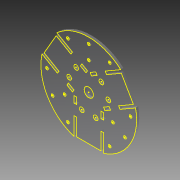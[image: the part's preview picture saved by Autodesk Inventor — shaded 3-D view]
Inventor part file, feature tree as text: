
AUTODESK INVENTOR PART (.ipt)
format: ipt  version: 2015 (Build 190159000, 159)  size: 303,616 bytes
history: native  units: mm
features: sketch x8, extrude x6, projected_geometry x4, pattern_circular x2
ambient origin geometry x8: Origin, YZ Plane, XZ Plane, XY Plane, X Axis, Y Axis, Z Axis, Center Point
bodies: Solid1 (feature_tree)
feature tree (20):
  extrude  "Extrusion1"  Depth=3.0mm TaperAngle=0.0deg
  extrude  "Extrusion2"  Depth=7.0mm
  extrude  "Extrusion3"  Depth=11.724mm
  extrude  "Extrusion4"  Depth=3.0mm
  extrude  "Extrusion5"  Depth=3.0mm TaperAngle=0.0deg
  pattern_circular  "Circular Pattern1"  [2 undecoded]
  sketch  "Sketch6"  dims[d12=5.0mm]
  pattern_circular  "Circular Pattern2"  [2 undecoded]
  extrude  "Extrusion6"  Depth=3.0mm TaperAngle=0.0deg
  sketch  "Sketch8"  dims[d14=20.006mm d15=5.0mm d16=3.0mm d17=0.0mm d18=3.0mm d19=0.0mm d20=48.0mm d21=10.0mm d22=3.0mm d23=0.0mm d24=30.0mm d25=360.0deg d27=30.0mm d28=360.0deg d30=60.0mm d31=90.0mm d32=30.0deg d33=30.0deg d34=30.0deg d35=30.0deg d36=30.0deg d37=30.0deg d38=120.0deg d39=120.0deg d40=3.0mm d41=3.0mm d42=3.0mm d43=3.0mm d44=3.0mm d45=3.0mm d46=3.0mm d47=3.0mm d48=3.0mm d49=3.0mm d50=3.0mm d51=3.0mm d52=3.0mm d53=0.0mm]
  sketch  "Sketch1"  dims[d0=103.0mm d1=3.0mm d2=0.0mm]
  sketch  "Sketch2"  dims[d3=10.906mm d4=7.0mm]
  projected_geometry  "Projected Loop1"
  sketch  "Sketch3"  dims[d5=11.724mm d6=40.0mm]
  sketch  "Sketch4"  dims[d7=32.0mm d8=3.0mm]
  projected_geometry  "Projected Loop2"
  sketch  "Sketch5"  dims[d9=3.0mm d10=3.0mm d11=0.0mm]
  sketch  "Sketch7"  dims[d13=15.0mm]
  projected_geometry  "Projected Loop3"
  projected_geometry  "Projected Loop4"
note: 4 required parameter values undecoded (feature->parameter linkage not recoverable at this tier; creation-order binding heuristic only, values carry confidence <= 0.55)
